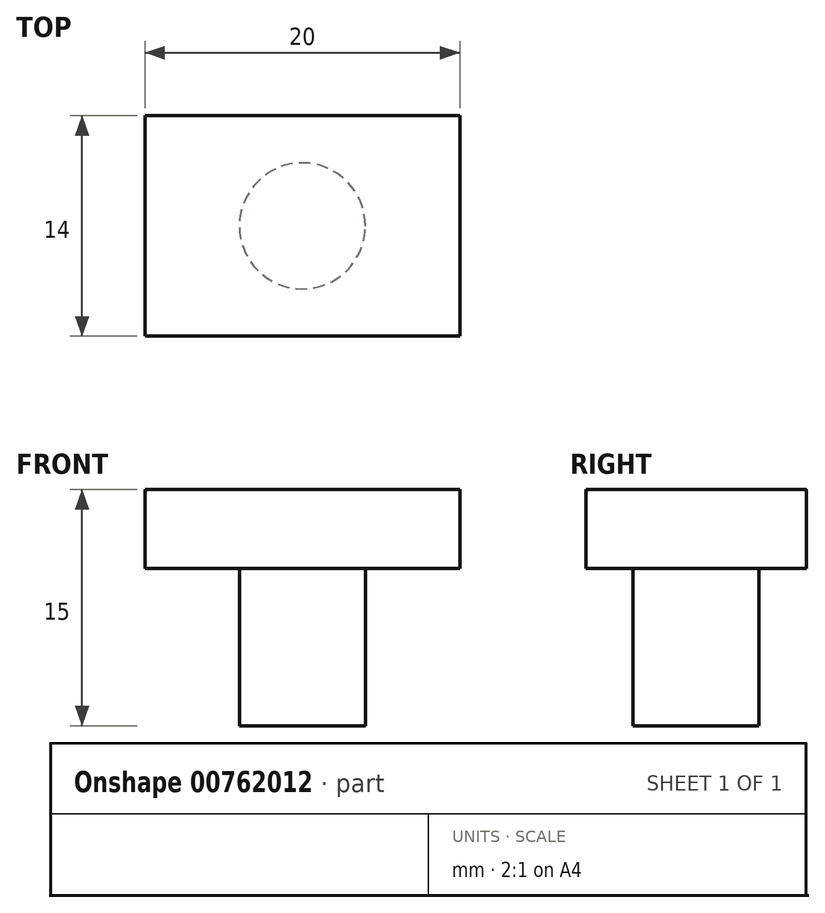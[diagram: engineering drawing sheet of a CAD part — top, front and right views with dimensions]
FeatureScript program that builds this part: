
annotation { "Feature Type Name" : "Feature", "Feature Type Description" : "" }
export const myFeature = defineFeature(function(context is Context, id is Id, definition is map)
    precondition{}
    {
        {
            var Q0;
            Q0=qCreatedBy(makeId("Top.planeOp"),FACE);
            var sketch = newSketch(context, id + "F0", { "sketchPlane" : qUnion([Q0])});
            skLineSegment(sketch, "E0.bottom", {"start": v(10, -7) * mm, "end": v(-10, -7) * mm});
            skLineSegment(sketch, "E0.top", {"start": v(10, 7) * mm, "end": v(-10, 7) * mm});
            skLineSegment(sketch, "E0.left", {"start": v(10, -7) * mm, "end": v(10, 7) * mm});
            skLineSegment(sketch, "E0.right", {"start": v(-10, -7) * mm, "end": v(-10, 7) * mm});
            skPoint(sketch, "E0.middle", {"position": v(0, 0) * mm});
            skCircle(sketch, "E1", {"center": v(0, 0) * mm, "radius": 4 * mm});
            skSolve(sketch);
        }
        {
            var Q0;
            Q0 = qSketchRegion(id + "F0", true);
            var Q1;
            Q1=makeQuery(id+"F0.imprint","IMPRINT",FACE,{"disambiguationData":[TD([[makeQuery(id+"F0.imprint","IMPRINT",EDGE,{"derivedFrom":sQuery(id+"F0.wireOp",EDGE,"E1")}),1.0]])]});
            extrude(context, id + "F1", {"entities" : qUnion([Q0, Q1]), "depth" : 5 * mm, "offsetDistance" : 25 * mm});
        }
        {
            var Q0;
            Q0=makeQuery(id+"F0.imprint","IMPRINT",FACE,{"disambiguationData":[TD([[makeQuery(id+"F0.imprint","IMPRINT",EDGE,{"derivedFrom":sQuery(id+"F0.wireOp",EDGE,"E1")}),1.0]])]});
            extrude(context, id + "F2", {"entities" : qUnion([Q0]), "operationType" : NewBodyOperationType.ADD, "oppositeDirection" : true, "depth" : 10 * mm, "offsetDistance" : 25 * mm});
        }
    });
